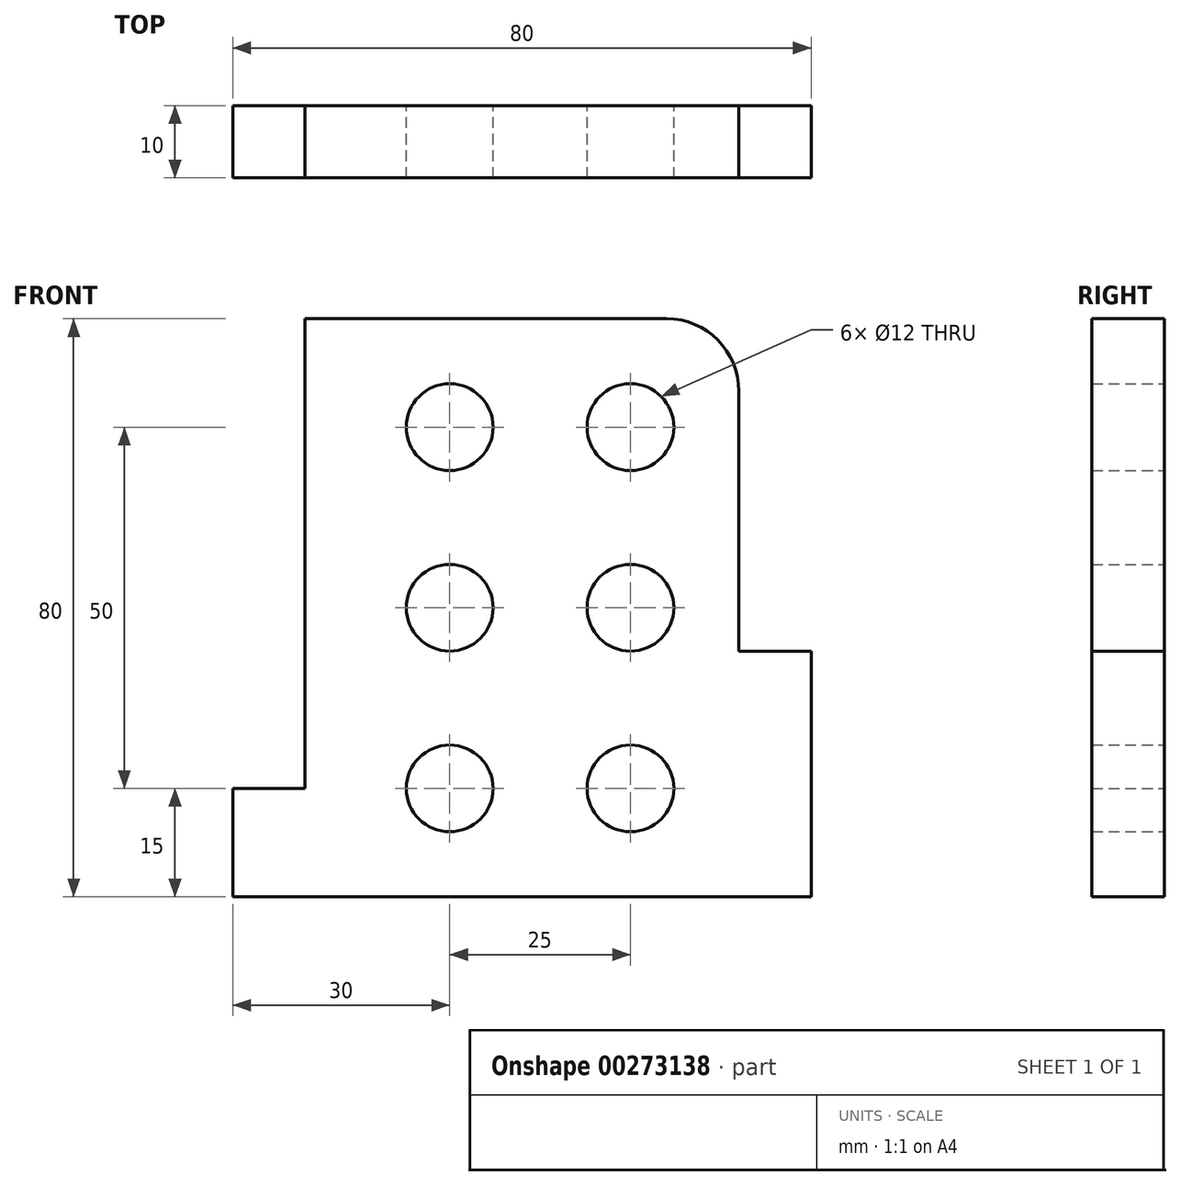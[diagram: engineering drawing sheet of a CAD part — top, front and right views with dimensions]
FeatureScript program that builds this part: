
annotation { "Feature Type Name" : "Feature", "Feature Type Description" : "" }
export const myFeature = defineFeature(function(context is Context, id is Id, definition is map)
    precondition{}
    {
        {
            var Q0;
            Q0=qCreatedBy(makeId("Front.planeOp"),FACE);
            var sketch = newSketch(context, id + "F0", { "sketchPlane" : qUnion([Q0])});
            skLineSegment(sketch, "E0", {"start": v(0, 0) * mm, "end": v(80, 0) * mm});
            skLineSegment(sketch, "E1", {"start": v(0, 0) * mm, "end": v(0, 15) * mm});
            skLineSegment(sketch, "E2", {"start": v(0, 15) * mm, "end": v(10, 15) * mm});
            skLineSegment(sketch, "E3", {"start": v(10, 15) * mm, "end": v(10, 80) * mm});
            skLineSegment(sketch, "E4", {"start": v(10, 80) * mm, "end": v(60, 80) * mm});
            skLineSegment(sketch, "E5", {"start": v(80, 0) * mm, "end": v(80, 34) * mm});
            skLineSegment(sketch, "E6", {"start": v(80, 34) * mm, "end": v(70, 34) * mm});
            skLineSegment(sketch, "E7", {"start": v(70, 34) * mm, "end": v(70, 70) * mm});
            skCircle(sketch, "E8", {"center": v(30, 15) * mm, "radius": 6 * mm});
            skCircle(sketch, "E9", {"center": v(30, 65) * mm, "radius": 6 * mm});
            skCircle(sketch, "E10", {"center": v(55, 65) * mm, "radius": 6 * mm});
            skCircle(sketch, "E11", {"center": v(55, 40) * mm, "radius": 6 * mm});
            skCircle(sketch, "E12", {"center": v(30, 40) * mm, "radius": 6 * mm});
            skCircle(sketch, "E13", {"center": v(55, 15) * mm, "radius": 6 * mm});
            skArc(sketch, "E14", {"start": v(70, 70) * mm, "mid": v(67.07, 77.07) * mm, "end": v(60, 80) * mm});
            skSolve(sketch);
        }
        {
            var Q0;
            Q0 = qSketchRegion(id + "F0", true);
            extrude(context, id + "F1", {"entities" : qUnion([Q0]), "depth" : 10 * mm});
        }
    });
